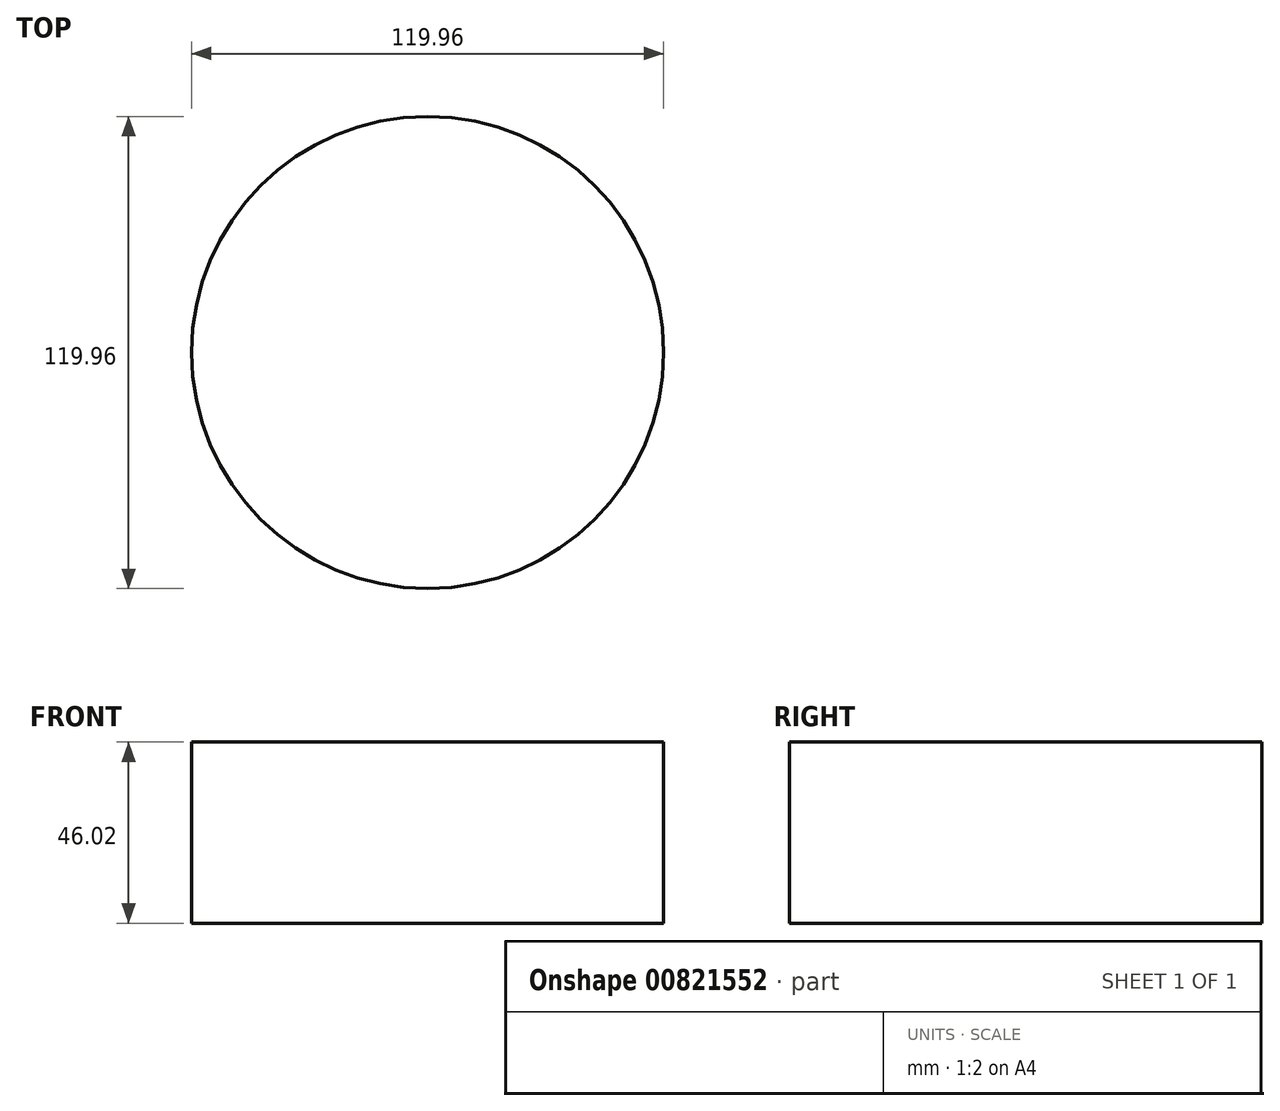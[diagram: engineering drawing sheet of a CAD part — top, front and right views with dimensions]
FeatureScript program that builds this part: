
annotation { "Feature Type Name" : "Feature", "Feature Type Description" : "" }
export const myFeature = defineFeature(function(context is Context, id is Id, definition is map)
    precondition{}
    {
        {
            var Q0;
            Q0=qCreatedBy(makeId("Top.planeOp"),FACE);
            var sketch = newSketch(context, id + "F0", { "sketchPlane" : qUnion([Q0])});
            skCircle(sketch, "E0", {"center": v(0, 0) * mm, "radius": 59.98 * mm});
            skSolve(sketch);
        }
        {
            var Q0;
            Q0=makeQuery(id+"F0.imprint","IMPRINT",FACE,{"disambiguationData":[TD([[makeQuery(id+"F0.imprint","IMPRINT",EDGE,{"derivedFrom":sQuery(id+"F0.wireOp",EDGE,"E0")}),1.0]])]});
            extrude(context, id + "F1", {"entities" : qUnion([Q0]), "depth" : 46.02 * mm, "offsetDistance" : 25.4 * mm});
        }
    });
